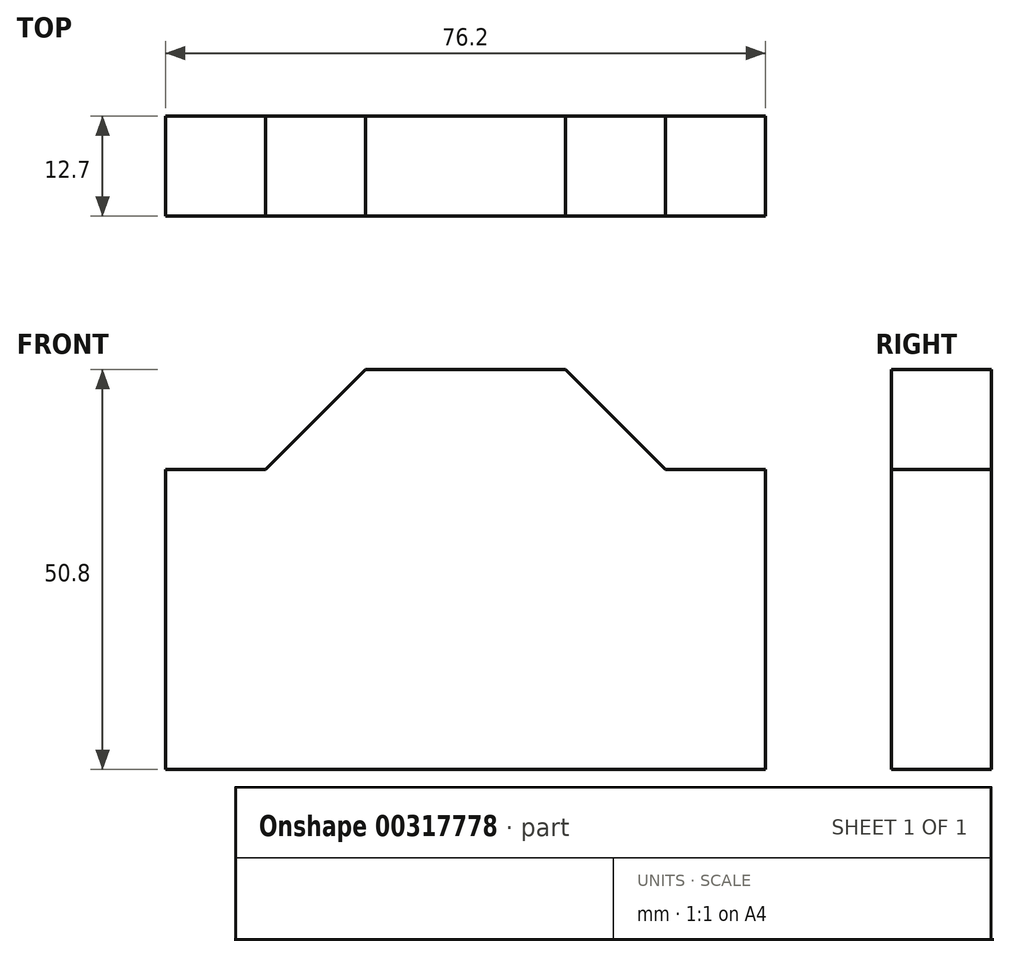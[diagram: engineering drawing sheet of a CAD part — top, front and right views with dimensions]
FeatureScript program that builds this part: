
annotation { "Feature Type Name" : "Feature", "Feature Type Description" : "" }
export const myFeature = defineFeature(function(context is Context, id is Id, definition is map)
    precondition{}
    {
        {
            var Q0;
            Q0=qCreatedBy(makeId("Top.planeOp"),FACE);
            var sketch = newSketch(context, id + "F0", { "sketchPlane" : qUnion([Q0])});
            skLineSegment(sketch, "E0", {"start": v(0, 0) * mm, "end": v(0, 50.8) * mm});
            skLineSegment(sketch, "E1", {"start": v(0, 50.8) * mm, "end": v(76.2, 50.8) * mm});
            skLineSegment(sketch, "E2", {"start": v(76.2, 50.8) * mm, "end": v(76.2, 0) * mm});
            skLineSegment(sketch, "E3", {"start": v(76.2, 0) * mm, "end": v(57.15, 0) * mm});
            skLineSegment(sketch, "E4", {"start": v(19.05, 0) * mm, "end": v(19.05, 12.7) * mm});
            skLineSegment(sketch, "E5", {"start": v(19.05, 12.7) * mm, "end": v(57.15, 12.7) * mm});
            skLineSegment(sketch, "E6", {"start": v(57.15, 12.7) * mm, "end": v(57.15, 0) * mm});
            skLineSegment(sketch, "E7.trimOffspring", {"start": v(19.05, 0) * mm, "end": v(0, 0) * mm});
            skLineSegment(sketch, "E8", {"start": v(0, 38.1) * mm, "end": v(76.2, 38.1) * mm});
            skLineSegment(sketch, "E9", {"start": v(76.2, 38.1) * mm, "end": v(76.2, 50.8) * mm});
            skLineSegment(sketch, "E10", {"start": v(0, 50.8) * mm, "end": v(0, 38.1) * mm});
            skSolve(sketch);
        }
        {
            var Q0;
            Q0=makeQuery(id+"F0.imprint","IMPRINT",FACE,{"disambiguationData":[TD([[makeQuery(id+"F0.imprint","IMPRINT",EDGE,{"derivedFrom":sQuery(id+"F0.wireOp",EDGE,"E1")}),-1.0]])]});
            extrude(context, id + "F1", {"entities" : qUnion([Q0]), "depth" : 50.8 * mm});
        }
        {
            var Q0;
            Q0=makeQuery(id+"F1.opExtrude","SWEPT_FACE",FACE,{"disambiguationData":[OSD([sQuery(id+"F0.wireOp",EDGE,"E1")])]});
            var sketch = newSketch(context, id + "F2", { "sketchPlane" : qUnion([Q0])});
            skLineSegment(sketch, "E11", {"start": v(-38.1, 50.8) * mm, "end": v(-38.1, -12.05) * mm, "construction": true});
            skLineSegment(sketch, "E12", {"start": v(-76.2, 50.8) * mm, "end": v(-50.8, 50.8) * mm});
            skLineSegment(sketch, "E13", {"start": v(-50.8, 50.8) * mm, "end": v(-76.2, 25.4) * mm});
            skLineSegment(sketch, "E14", {"start": v(-76.2, 25.4) * mm, "end": v(-76.2, 50.8) * mm});
            skLineSegment(sketch, "E15.MirrorCS", {"start": v(-25.4, 50.8) * mm, "end": v(0, 25.4) * mm});
            skLineSegment(sketch, "E16.MirrorCS", {"start": v(0, 50.8) * mm, "end": v(-25.4, 50.8) * mm});
            skLineSegment(sketch, "E17.MirrorCS", {"start": v(0, 25.4) * mm, "end": v(0, 50.8) * mm});
            skSolve(sketch);
        }
        {
            var Q0;
            Q0=makeQuery(id+"F2.imprint","IMPRINT",FACE,{"disambiguationData":[TD([[makeQuery(id+"F2.imprint","IMPRINT",EDGE,{"derivedFrom":sQuery(id+"F2.wireOp",EDGE,"E15.MirrorCS")}),1.0]])]});
            extrude(context, id + "F3", {"entities" : qUnion([Q0]), "operationType" : NewBodyOperationType.REMOVE, "oppositeDirection" : true, "depth" : 25.4 * mm});
        }
        {
            var Q0;
            Q0=makeQuery(id+"F2.imprint","IMPRINT",FACE,{"disambiguationData":[TD([[makeQuery(id+"F2.imprint","IMPRINT",EDGE,{"derivedFrom":sQuery(id+"F2.wireOp",EDGE,"E12")}),1.0]])]});
            extrude(context, id + "F4", {"entities" : qUnion([Q0]), "operationType" : NewBodyOperationType.REMOVE, "oppositeDirection" : true, "depth" : 25.4 * mm});
        }
        {
            var Q0;
            Q0=makeQuery(id+"F0.imprint","IMPRINT",FACE,{"disambiguationData":[TD([[makeQuery(id+"F0.imprint","IMPRINT",EDGE,{"derivedFrom":sQuery(id+"F0.wireOp",EDGE,"E0")}),-1.0]])]});
            extrude(context, id + "F5", {"entities" : qUnion([Q0]), "operationType" : NewBodyOperationType.ADD, "depth" : 38.1 * mm});
        }
        {
            var Q0;
            Q0=makeQuery(id+"F5.boolean.opBoolean","MERGE",FACE,{"derivedFrom":[makeQuery(id+"F1.opExtrude","SWEPT_FACE",FACE,{"disambiguationData":[OSD([sQuery(id+"F0.wireOp",EDGE,"E9")])]}),makeQuery(id+"F5.opExtrude","SWEPT_FACE",FACE,{"disambiguationData":[OSD([sQuery(id+"F0.wireOp",EDGE,"E2")])]})]});
            var sketch = newSketch(context, id + "F6", { "sketchPlane" : qUnion([Q0])});
            skLineSegment(sketch, "E18", {"start": v(38.1, 38.1) * mm, "end": v(0, 0) * mm});
            skLineSegment(sketch, "E19", {"start": v(0, 0) * mm, "end": v(0, 38.1) * mm});
            skLineSegment(sketch, "E20", {"start": v(0, 38.1) * mm, "end": v(38.1, 38.1) * mm});
            skSolve(sketch);
        }
        {
            var Q0;
            Q0=makeQuery(id+"F6.imprint","IMPRINT",FACE,{"disambiguationData":[TD([[makeQuery(id+"F6.imprint","IMPRINT",EDGE,{"derivedFrom":sQuery(id+"F6.wireOp",EDGE,"E18")}),-1.0]])]});
            extrude(context, id + "F7", {"entities" : qUnion([Q0]), "operationType" : NewBodyOperationType.REMOVE, "endBound" : BoundingType.THROUGH_ALL, "oppositeDirection" : true, "depth" : 25.4 * mm});
        }
        {
            var Q0;
            Q0=qCreatedBy(makeId("Front.planeOp"),FACE);
            var sketch = newSketch(context, id + "F8", { "sketchPlane" : qUnion([Q0])});
            skLineSegment(sketch, "E21", {"start": v(0, 0) * mm, "end": v(76.2, 0) * mm});
            skLineSegment(sketch, "E22", {"start": v(76.2, 0) * mm, "end": v(38.1, 38.1) * mm});
            skLineSegment(sketch, "E23", {"start": v(38.1, 38.1) * mm, "end": v(0, 0) * mm});
            skLineSegment(sketch, "E24", {"start": v(38.1, 38.1) * mm, "end": v(0, 38.1) * mm});
            skLineSegment(sketch, "E25", {"start": v(0, 38.1) * mm, "end": v(0, 0) * mm});
            skLineSegment(sketch, "E26", {"start": v(38.1, 38.1) * mm, "end": v(76.2, 38.1) * mm});
            skLineSegment(sketch, "E27", {"start": v(76.2, 38.1) * mm, "end": v(76.2, 0) * mm});
            skSolve(sketch);
        }
        {
            var Q0;
            Q0=makeQuery(id+"F8.imprint","IMPRINT",FACE,{"disambiguationData":[TD([[makeQuery(id+"F8.imprint","IMPRINT",EDGE,{"derivedFrom":sQuery(id+"F8.wireOp",EDGE,"E22")}),-1.0]])]});
            extrude(context, id + "F9", {"entities" : qUnion([Q0]), "operationType" : NewBodyOperationType.REMOVE, "oppositeDirection" : true, "depth" : 38.1 * mm});
        }
        {
            var Q0;
            Q0=makeQuery(id+"F8.imprint","IMPRINT",FACE,{"disambiguationData":[TD([[makeQuery(id+"F8.imprint","IMPRINT",EDGE,{"derivedFrom":sQuery(id+"F8.wireOp",EDGE,"E23")}),-1.0]])]});
            extrude(context, id + "F10", {"entities" : qUnion([Q0]), "operationType" : NewBodyOperationType.REMOVE, "oppositeDirection" : true, "depth" : 38.1 * mm});
        }
    });
